# Revit family: Клапан постоянного расхода КПРП
name_source: partatom
category: Арматура воздуховодов
units: mm (PartAtom-declared; Revit-internal decimal feet)

## family parameters
Всегда вертикально = Да
На основе рабочей плоскости = Нет
Общий = Нет
При загрузке вырезать с полостями = Нет
Размер круглого соединителя = Использовать диаметр
Тип детали = Вставляется

## types (2) — shared parameters
ADSK_Единица измерения = шт
ADSK_Завод-изготовитель = Veox
ADSK_Материал = ANJ010013
ADSK_Обозначение = VRC-N D100
URL = https://veox.ru
Группа модели = клапан круглый
Доп уго на 3д виде = Да
Изготовитель = Veox
КМС = 1
тип = 2
zero-valued in all types: Отметка по умолчанию

## per-type parameters (varying)
| type | ADSK_Марка | ADSK_Наименование | ADSK_Размер_Длина | Длина клапана | ИНЖ_Диаметр 1 |
| DN100 | КПРП D100 | Клапан постоянного расхода воздуха пластиковый КПРП, D100 | 100 мм | 100 мм | 100 мм |
| DN125 | КПРП D25 | Клапан постоянного расхода воздуха пластиковый КПРП, D125 | 118 мм | 118 мм | 125 мм |

## geometry (parser evidence)
native form markers: Sweep x2
no freeform markers — native parametric forms only
